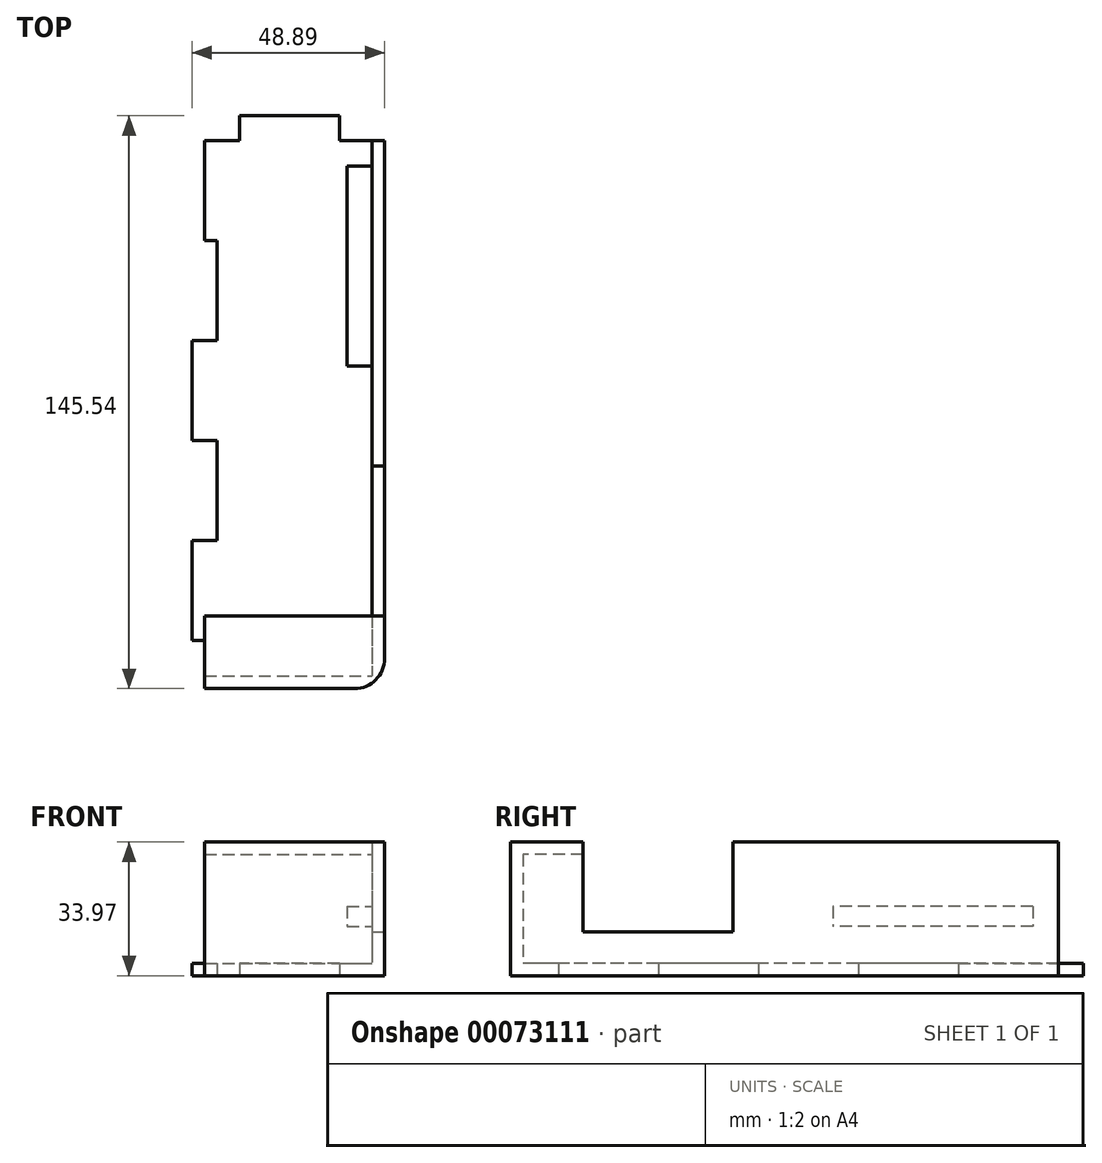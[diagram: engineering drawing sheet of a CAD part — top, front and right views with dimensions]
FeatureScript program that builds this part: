
annotation { "Feature Type Name" : "Feature", "Feature Type Description" : "" }
export const myFeature = defineFeature(function(context is Context, id is Id, definition is map)
    precondition{}
    {
        {
            var Q0;
            Q0=qCreatedBy(makeId("Top.planeOp"),FACE);
            var sketch = newSketch(context, id + "F0", { "sketchPlane" : qUnion([Q0])});
            skLineSegment(sketch, "E0.bottom", {"start": v(-19.05, 109.54) * mm, "end": v(-10.16, 109.54) * mm});
            skLineSegment(sketch, "E0.top", {"start": v(-19.05, -29.65) * mm, "end": v(26.67, -29.65) * mm});
            skLineSegment(sketch, "E0.right", {"start": v(26.67, 109.54) * mm, "end": v(26.67, -29.65) * mm});
            skLineSegment(sketch, "E1.bottom", {"start": v(-19.05, 84.14) * mm, "end": v(-15.87, 84.14) * mm});
            skLineSegment(sketch, "E1.top", {"start": v(-19.05, 58.74) * mm, "end": v(-15.87, 58.74) * mm});
            skLineSegment(sketch, "E1.right", {"start": v(-15.87, 84.14) * mm, "end": v(-15.87, 58.74) * mm});
            skLineSegment(sketch, "E2.0.1.1", {"start": v(-19.05, 33.34) * mm, "end": v(-15.87, 33.34) * mm});
            skLineSegment(sketch, "E2.0.1.2", {"start": v(-15.87, 33.34) * mm, "end": v(-15.87, 7.94) * mm});
            skLineSegment(sketch, "E2.0.1.3", {"start": v(-19.05, 7.94) * mm, "end": v(-15.87, 7.94) * mm});
            skLineSegment(sketch, "E2.direction1", {"start": v(-19.05, 58.74) * mm, "end": v(6.35, 58.74) * mm, "construction": true});
            skLineSegment(sketch, "E2.direction2", {"start": v(-19.05, 58.74) * mm, "end": v(-19.05, 7.94) * mm, "construction": true});
            skLineSegment(sketch, "E3.bottom", {"start": v(-19.05, 109.54) * mm, "end": v(-22.22, 109.54) * mm});
            skLineSegment(sketch, "E3.top", {"start": v(-19.05, 84.14) * mm, "end": v(-22.22, 84.14) * mm});
            skLineSegment(sketch, "E4.0.1.0", {"start": v(-19.05, 58.74) * mm, "end": v(-22.22, 58.74) * mm});
            skLineSegment(sketch, "E4.0.1.1", {"start": v(-22.22, 58.74) * mm, "end": v(-22.22, 33.34) * mm});
            skLineSegment(sketch, "E4.0.1.2", {"start": v(-19.05, 33.34) * mm, "end": v(-22.22, 33.34) * mm});
            skLineSegment(sketch, "E4.direction1", {"start": v(-22.22, 109.54) * mm, "end": v(3.18, 109.54) * mm, "construction": true});
            skLineSegment(sketch, "E4.direction2", {"start": v(-22.22, 109.54) * mm, "end": v(-22.22, 58.74) * mm, "construction": true});
            skLineSegment(sketch, "E5", {"start": v(-19.05, 84.14) * mm, "end": v(-19.05, 109.54) * mm});
            skLineSegment(sketch, "E6.0.0.2", {"start": v(-19.05, 7.94) * mm, "end": v(-22.22, 7.94) * mm});
            skLineSegment(sketch, "E6.3.0.2", {"start": v(-22.22, 7.94) * mm, "end": v(-22.22, -17.46) * mm});
            skLineSegment(sketch, "E6.6.0.2", {"start": v(-19.05, -17.46) * mm, "end": v(-22.22, -17.46) * mm});
            skLineSegment(sketch, "E7", {"start": v(-19.05, -17.46) * mm, "end": v(-19.05, -29.65) * mm});
            skLineSegment(sketch, "E8.top", {"start": v(15.24, 115.89) * mm, "end": v(-10.16, 115.89) * mm});
            skLineSegment(sketch, "E8.left", {"start": v(15.24, 109.54) * mm, "end": v(15.24, 115.89) * mm});
            skLineSegment(sketch, "E8.right", {"start": v(-10.16, 109.54) * mm, "end": v(-10.16, 115.89) * mm});
            skLineSegment(sketch, "E9", {"start": v(15.24, 109.54) * mm, "end": v(26.67, 109.54) * mm});
            skSolve(sketch);
        }
        {
            var Q0;
            {var subQ1=sQuery(id+"F0.wireOp",EDGE,"E0.bottom");Q0=makeQuery(id+"F0.imprint","IMPRINT",FACE,{"disambiguationData":[TD([[makeQuery(id+"F0.imprint","IMPRINT",EDGE,{"derivedFrom":subQ1}),-1.0]])]});}
            extrude(context, id + "F1", {"entities" : qUnion([Q0]), "depth" : 3.17 * mm});
        }
        {
            var Q0;
            Q0=makeQuery(id+"F1.opExtrude","CAP_FACE",FACE,{"disambiguationData":[OSD([sQuery(id+"F0.wireOp",EDGE,"E0.bottom"),sQuery(id+"F0.wireOp",EDGE,"E0.top"),sQuery(id+"F0.wireOp",EDGE,"E0.left"),sQuery(id+"F0.wireOp",EDGE,"E0.right"),sQuery(id+"F0.wireOp",EDGE,"E1.bottom"),sQuery(id+"F0.wireOp",EDGE,"E1.top"),sQuery(id+"F0.wireOp",EDGE,"E1.right"),sQuery(id+"F0.wireOp",EDGE,"E2.0.1.1"),sQuery(id+"F0.wireOp",EDGE,"E2.0.1.2"),sQuery(id+"F0.wireOp",EDGE,"E2.0.1.3"),sQuery(id+"F0.wireOp",EDGE,"E2.0.2.1"),sQuery(id+"F0.wireOp",EDGE,"E2.0.2.2"),sQuery(id+"F0.wireOp",EDGE,"E2.0.2.3")])],"isStart":false});
            var sketch = newSketch(context, id + "F2", { "sketchPlane" : qUnion([Q0])});
            skLineSegment(sketch, "E10.0", {"start": v(-19.05, -26.48) * mm, "end": v(23.5, -26.48) * mm});
            skLineSegment(sketch, "E10.1", {"start": v(23.5, 109.54) * mm, "end": v(23.5, -26.48) * mm});
            skSolve(sketch);
        }
        {
            var Q0;
            {var subQ5=sQuery(id+"F2.wireOp",EDGE,"E10.0");Q0=makeQuery(id+"F2.imprint","IMPRINT",FACE,{"disambiguationData":[TD([[makeQuery(id+"F2.imprint","IMPRINT",EDGE,{"derivedFrom":subQ5}),-1.0]])]});}
            extrude(context, id + "F3", {"entities" : qUnion([Q0]), "operationType" : NewBodyOperationType.ADD, "depth" : 30.8 * mm});
        }
        {
            var Q0;
            Q0=makeQuery(id+"F3.opExtrude","CAP_FACE",FACE,{"disambiguationData":[OSD([sQuery(id+"F0.wireOp",EDGE,"E0.bottom"),sQuery(id+"F0.wireOp",EDGE,"E0.top"),sQuery(id+"F0.wireOp",EDGE,"E0.left"),sQuery(id+"F0.wireOp",EDGE,"E0.right"),sQuery(id+"F2.wireOp",EDGE,"E10.0"),sQuery(id+"F2.wireOp",EDGE,"E10.1")])],"isStart":false});
            var sketch = newSketch(context, id + "F4", { "sketchPlane" : qUnion([Q0])});
            skLineSegment(sketch, "E11.bottom", {"start": v(-19.05, -26.48) * mm, "end": v(23.5, -26.48) * mm});
            skLineSegment(sketch, "E11.top", {"start": v(-19.05, -11.24) * mm, "end": v(23.5, -11.24) * mm});
            skLineSegment(sketch, "E11.left", {"start": v(-19.05, -26.48) * mm, "end": v(-19.05, -11.24) * mm});
            skLineSegment(sketch, "E11.right", {"start": v(23.5, -26.48) * mm, "end": v(23.5, -11.24) * mm});
            skSolve(sketch);
        }
        {
            var Q0;
            Q0 = qSketchRegion(id + "F4", true);
            extrude(context, id + "F5", {"entities" : qUnion([Q0]), "operationType" : NewBodyOperationType.ADD, "oppositeDirection" : true, "depth" : 3.17 * mm});
        }
        {
            var Q0;
            {var subQ0=sQuery(id+"F0.wireOp",EDGE,"E0.right");Q0=makeQuery(id+"F3.boolean.opBoolean","MERGE",FACE,{"derivedFrom":[makeQuery(id+"F1.opExtrude","SWEPT_FACE",FACE,{"disambiguationData":[OSD([subQ0])]}),makeQuery(id+"F3.opExtrude","SWEPT_FACE",FACE,{"disambiguationData":[OSD([subQ0])]})]});}
            var sketch = newSketch(context, id + "F6", { "sketchPlane" : qUnion([Q0])});
            skLineSegment(sketch, "E12.bottom", {"start": v(-11.24, 33.97) * mm, "end": v(26.86, 33.97) * mm});
            skLineSegment(sketch, "E12.top", {"start": v(-11.24, 11.11) * mm, "end": v(26.86, 11.11) * mm});
            skLineSegment(sketch, "E12.left", {"start": v(-11.24, 33.97) * mm, "end": v(-11.24, 11.11) * mm});
            skLineSegment(sketch, "E12.right", {"start": v(26.86, 33.97) * mm, "end": v(26.86, 11.11) * mm});
            skSolve(sketch);
        }
        {
            var Q0;
            Q0=makeQuery(id+"F6.imprint","IMPRINT",FACE,{"disambiguationData":[TD([[makeQuery(id+"F6.imprint","IMPRINT",EDGE,{"derivedFrom":sQuery(id+"F6.wireOp",EDGE,"E12.bottom")}),1.0]])]});
            extrude(context, id + "F7", {"entities" : qUnion([Q0]), "operationType" : NewBodyOperationType.REMOVE, "endBound" : BoundingType.THROUGH_ALL, "oppositeDirection" : true, "depth" : 25.4 * mm});
        }
        {
            var Q0;
            Q0=makeQuery(id+"F3.opExtrude","SWEPT_FACE",FACE,{"disambiguationData":[OSD([sQuery(id+"F2.wireOp",EDGE,"E10.1")])]});
            var sketch = newSketch(context, id + "F8", { "sketchPlane" : qUnion([Q0])});
            skLineSegment(sketch, "E13.bottom", {"start": v(-103.06, 17.62) * mm, "end": v(-52.26, 17.62) * mm});
            skLineSegment(sketch, "E13.top", {"start": v(-103.06, 12.54) * mm, "end": v(-52.26, 12.54) * mm});
            skLineSegment(sketch, "E13.left", {"start": v(-103.06, 17.62) * mm, "end": v(-103.06, 12.54) * mm});
            skLineSegment(sketch, "E13.right", {"start": v(-52.26, 17.62) * mm, "end": v(-52.26, 12.54) * mm});
            skSolve(sketch);
        }
        {
            var Q0;
            Q0=makeQuery(id+"F8.imprint","IMPRINT",FACE,{"disambiguationData":[TD([[makeQuery(id+"F8.imprint","IMPRINT",EDGE,{"derivedFrom":sQuery(id+"F8.wireOp",EDGE,"E13.bottom")}),-1.0]])]});
            extrude(context, id + "F9", {"entities" : qUnion([Q0]), "operationType" : NewBodyOperationType.ADD, "depth" : 6.35 * mm});
        }
        {
            var Q0;
            {var subQ0=sQuery(id+"F0.wireOp",EDGE,"E0.right");var subQ1=sQuery(id+"F0.wireOp",EDGE,"E0.top");Q0=makeQuery(id+"F3.boolean.opBoolean","MERGE",EDGE,{"derivedFrom":[makeQuery(id+"F1.opExtrude","SWEPT_EDGE",EDGE,{"disambiguationData":[OSD([subQ1,subQ0])]}),makeQuery(id+"F3.opExtrude","SWEPT_EDGE",EDGE,{"disambiguationData":[OSD([subQ1,subQ0])]})]});}
            fillet(context, id + "F10", {"entities" : qUnion([Q0]), "radius" : 7.62 * mm, "tangentPropagation" : true, "allowEdgeOverflow" : false});
        }
    });
